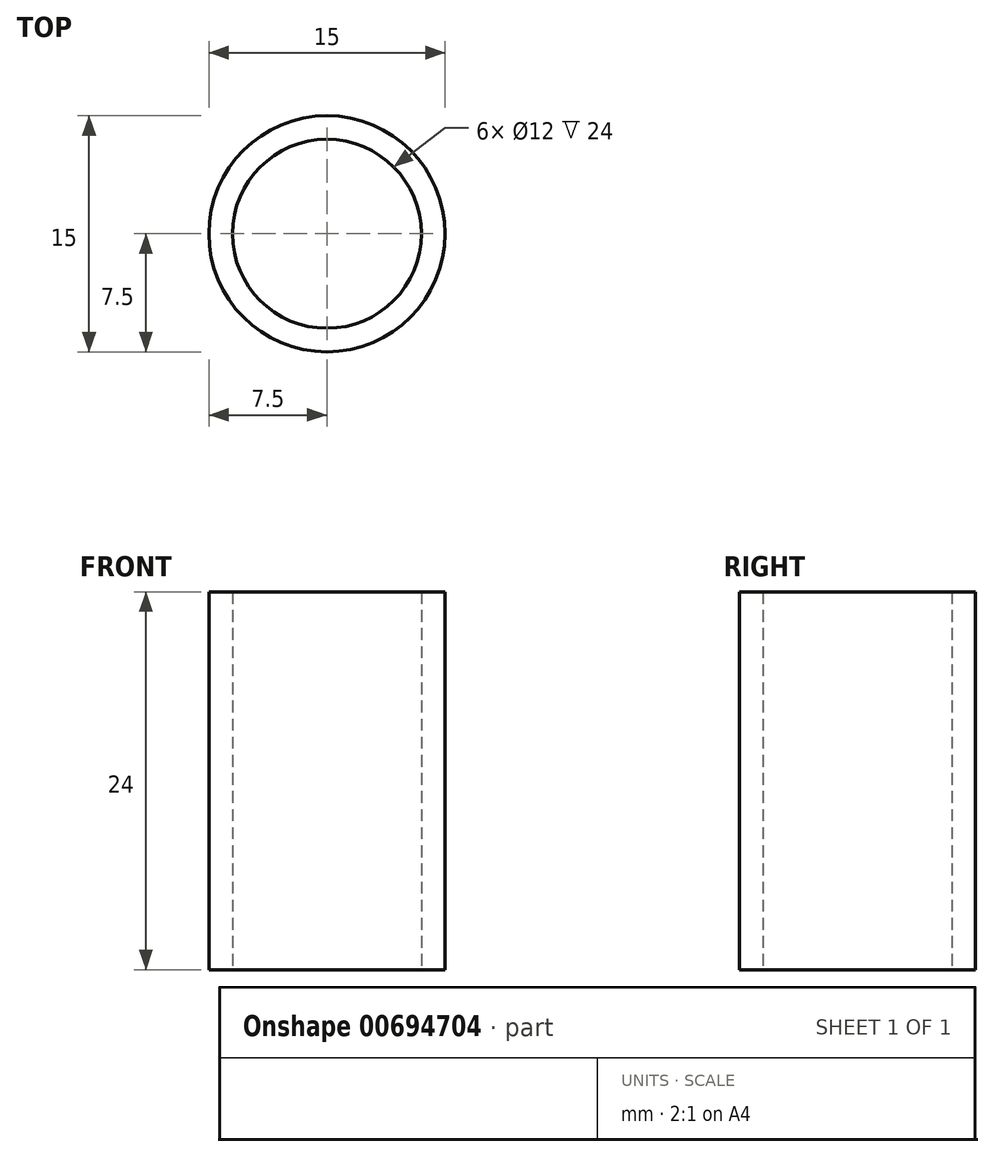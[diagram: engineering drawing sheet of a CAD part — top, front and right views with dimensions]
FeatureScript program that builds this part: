
annotation { "Feature Type Name" : "Feature", "Feature Type Description" : "" }
export const myFeature = defineFeature(function(context is Context, id is Id, definition is map)
    precondition{}
    {
        {
            var Q0;
            Q0=qCreatedBy(makeId("Top.planeOp"),FACE);
            var sketch = newSketch(context, id + "F0", { "sketchPlane" : qUnion([Q0])});
            skCircle(sketch, "E0", {"center": v(0, 0) * mm, "radius": 7.5 * mm});
            skCircle(sketch, "E1", {"center": v(0, 0) * mm, "radius": 6 * mm});
            skSolve(sketch);
        }
        {
            var Q0;
            Q0=makeQuery(id+"F0.imprint","IMPRINT",FACE,{"disambiguationData":[TD([[makeQuery(id+"F0.imprint","IMPRINT",EDGE,{"derivedFrom":sQuery(id+"F0.wireOp",EDGE,"E0")}),1.0]])]});
            extrude(context, id + "F1", {"entities" : qUnion([Q0]), "depth" : 24 * mm, "offsetDistance" : 25 * mm});
        }
    });
